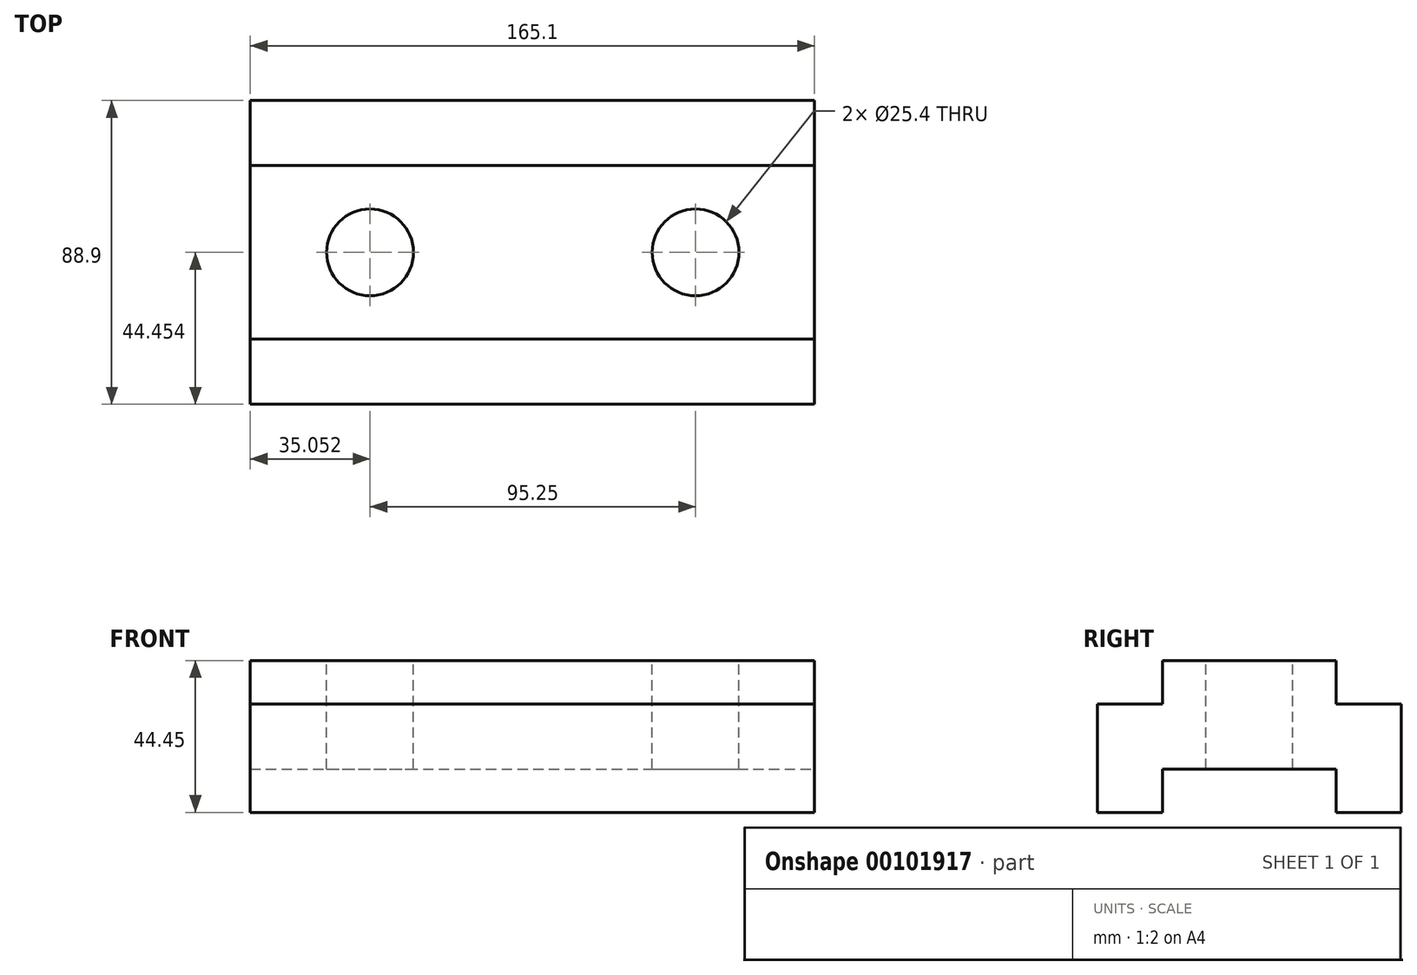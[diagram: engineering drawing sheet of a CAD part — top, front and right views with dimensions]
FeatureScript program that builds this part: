
annotation { "Feature Type Name" : "Feature", "Feature Type Description" : "" }
export const myFeature = defineFeature(function(context is Context, id is Id, definition is map)
    precondition{}
    {
        {
            var Q0;
            Q0=qCreatedBy(makeId("Right.planeOp"),FACE);
            var sketch = newSketch(context, id + "F0", { "sketchPlane" : qUnion([Q0])});
            skLineSegment(sketch, "E0.bottom", {"start": v(-37.98, 14) * mm, "end": v(50.92, 14) * mm});
            skLineSegment(sketch, "E0.top", {"start": v(-37.98, -30.46) * mm, "end": v(50.92, -30.46) * mm});
            skLineSegment(sketch, "E0.left", {"start": v(-37.98, 14) * mm, "end": v(-37.98, -30.46) * mm});
            skLineSegment(sketch, "E0.right", {"start": v(50.92, 14) * mm, "end": v(50.92, -30.46) * mm});
            skSolve(sketch);
        }
        {
            var Q0;
            Q0 = qSketchRegion(id + "F0", true);
            extrude(context, id + "F1", {"entities" : qUnion([Q0]), "oppositeDirection" : true, "depth" : 165.1 * mm});
        }
        {
            var Q0;
            Q0=makeQuery(id+"F1.opExtrude","CAP_FACE",FACE,{"disambiguationData":[OSD([sQuery(id+"F0.wireOp",EDGE,"E0.bottom"),sQuery(id+"F0.wireOp",EDGE,"E0.top"),sQuery(id+"F0.wireOp",EDGE,"E0.left"),sQuery(id+"F0.wireOp",EDGE,"E0.right")])],"isStart":true});
            var sketch = newSketch(context, id + "F2", { "sketchPlane" : qUnion([Q0])});
            skLineSegment(sketch, "E1.bottom", {"start": v(-18.93, -30.46) * mm, "end": v(31.87, -30.46) * mm});
            skLineSegment(sketch, "E1.top", {"start": v(-18.93, -17.76) * mm, "end": v(31.87, -17.76) * mm});
            skLineSegment(sketch, "E1.left", {"start": v(-18.93, -30.46) * mm, "end": v(-18.93, -17.76) * mm});
            skLineSegment(sketch, "E1.right", {"start": v(31.87, -30.46) * mm, "end": v(31.87, -17.76) * mm});
            skSolve(sketch);
        }
        {
            var Q0;
            Q0 = qSketchRegion(id + "F2", true);
            extrude(context, id + "F3", {"entities" : qUnion([Q0]), "operationType" : NewBodyOperationType.REMOVE, "oppositeDirection" : true, "depth" : 165.1 * mm});
        }
        {
            var Q0;
            Q0=makeQuery(id+"F1.opExtrude","CAP_FACE",FACE,{"disambiguationData":[OSD([sQuery(id+"F0.wireOp",EDGE,"E0.bottom"),sQuery(id+"F0.wireOp",EDGE,"E0.top"),sQuery(id+"F0.wireOp",EDGE,"E0.left"),sQuery(id+"F0.wireOp",EDGE,"E0.right")])],"isStart":true});
            var sketch = newSketch(context, id + "F4", { "sketchPlane" : qUnion([Q0])});
            skLineSegment(sketch, "E2.bottom", {"start": v(50.92, 14) * mm, "end": v(31.87, 14) * mm});
            skLineSegment(sketch, "E2.top", {"start": v(50.92, 1.3) * mm, "end": v(31.87, 1.3) * mm});
            skLineSegment(sketch, "E2.left", {"start": v(50.92, 14) * mm, "end": v(50.92, 1.3) * mm});
            skLineSegment(sketch, "E2.right", {"start": v(31.87, 14) * mm, "end": v(31.87, 1.3) * mm});
            skLineSegment(sketch, "E3.bottom", {"start": v(-37.98, 14) * mm, "end": v(-18.93, 14) * mm});
            skLineSegment(sketch, "E3.top", {"start": v(-37.98, 1.3) * mm, "end": v(-18.93, 1.3) * mm});
            skLineSegment(sketch, "E3.left", {"start": v(-37.98, 14) * mm, "end": v(-37.98, 1.3) * mm});
            skLineSegment(sketch, "E3.right", {"start": v(-18.93, 14) * mm, "end": v(-18.93, 1.3) * mm});
            skSolve(sketch);
        }
        {
            var Q0;
            Q0 = qSketchRegion(id + "F4", true);
            extrude(context, id + "F5", {"entities" : qUnion([Q0]), "operationType" : NewBodyOperationType.REMOVE, "oppositeDirection" : true, "depth" : 165.1 * mm});
        }
        {
            var Q0;
            Q0=makeQuery(id+"F1.opExtrude","SWEPT_FACE",FACE,{"disambiguationData":[OSD([sQuery(id+"F0.wireOp",EDGE,"E0.bottom")])]});
            var sketch = newSketch(context, id + "F6", { "sketchPlane" : qUnion([Q0])});
            skCircle(sketch, "E4", {"center": v(-130.05, 6.47) * mm, "radius": 12.7 * mm});
            skCircle(sketch, "E5", {"center": v(-34.8, 6.47) * mm, "radius": 12.7 * mm});
            skSolve(sketch);
        }
        {
            var Q0;
            Q0 = qSketchRegion(id + "F6", true);
            extrude(context, id + "F7", {"entities" : qUnion([Q0]), "operationType" : NewBodyOperationType.REMOVE, "oppositeDirection" : true, "depth" : 44.45 * mm});
        }
    });
